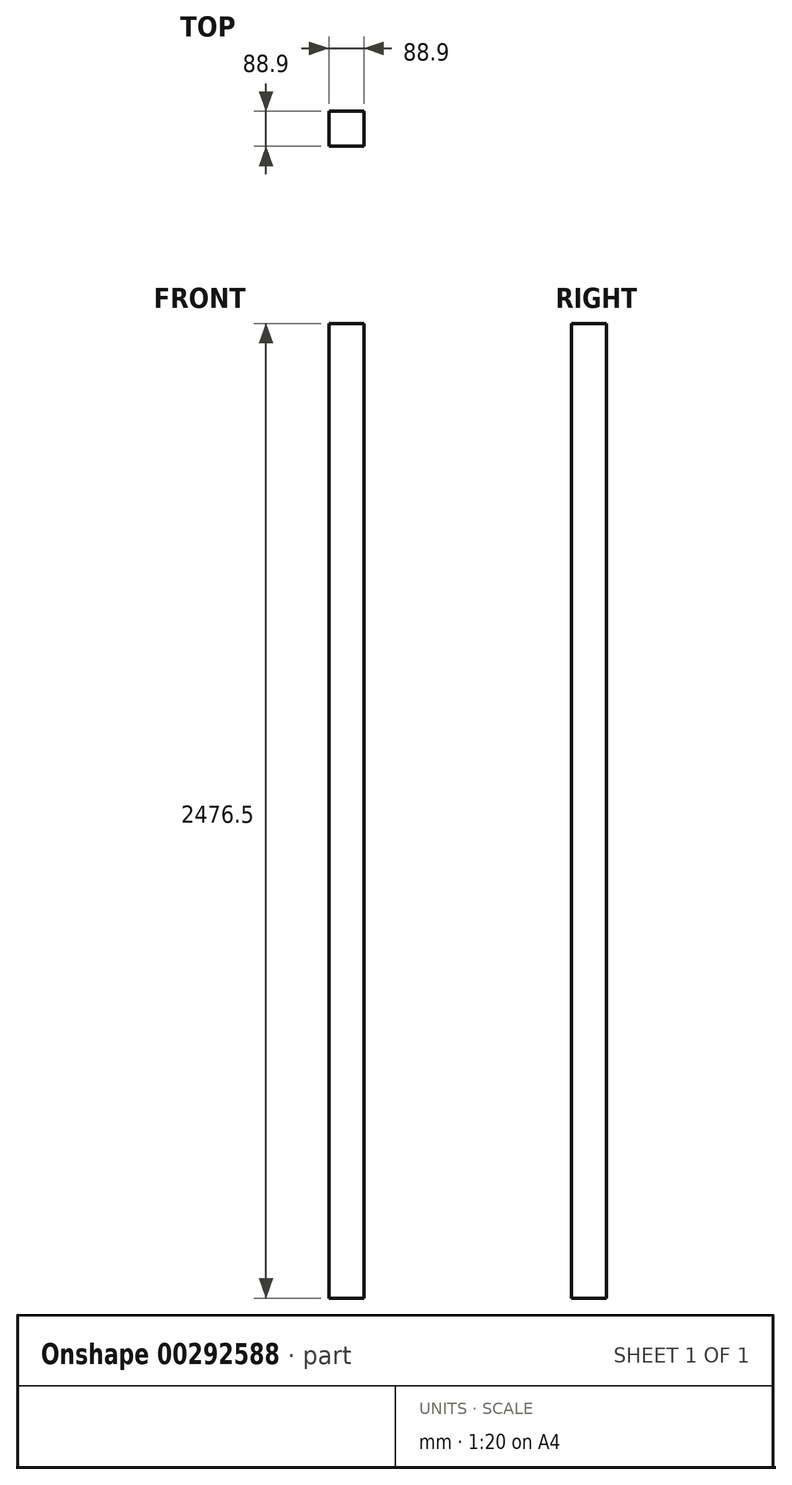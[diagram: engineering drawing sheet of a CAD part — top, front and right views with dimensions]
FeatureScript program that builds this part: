
annotation { "Feature Type Name" : "Feature", "Feature Type Description" : "" }
export const myFeature = defineFeature(function(context is Context, id is Id, definition is map)
    precondition{}
    {
        {
            var Q0;
            Q0=qCreatedBy(makeId("Top.planeOp"),FACE);
            var sketch = newSketch(context, id + "F0", { "sketchPlane" : qUnion([Q0])});
            skLineSegment(sketch, "E0.bottom", {"start": v(44.45, 44.45) * mm, "end": v(-44.45, 44.45) * mm});
            skLineSegment(sketch, "E0.top", {"start": v(44.45, -44.45) * mm, "end": v(-44.45, -44.45) * mm});
            skLineSegment(sketch, "E0.left", {"start": v(44.45, 44.45) * mm, "end": v(44.45, -44.45) * mm});
            skLineSegment(sketch, "E0.right", {"start": v(-44.45, 44.45) * mm, "end": v(-44.45, -44.45) * mm});
            skPoint(sketch, "E0.middle", {"position": v(0, 0) * mm});
            skSolve(sketch);
        }
        {
            var Q0;
            Q0 = qSketchRegion(id + "F0", true);
            extrude(context, id + "F1", {"entities" : qUnion([Q0]), "depth" : 2476.5 * mm});
        }
    });
